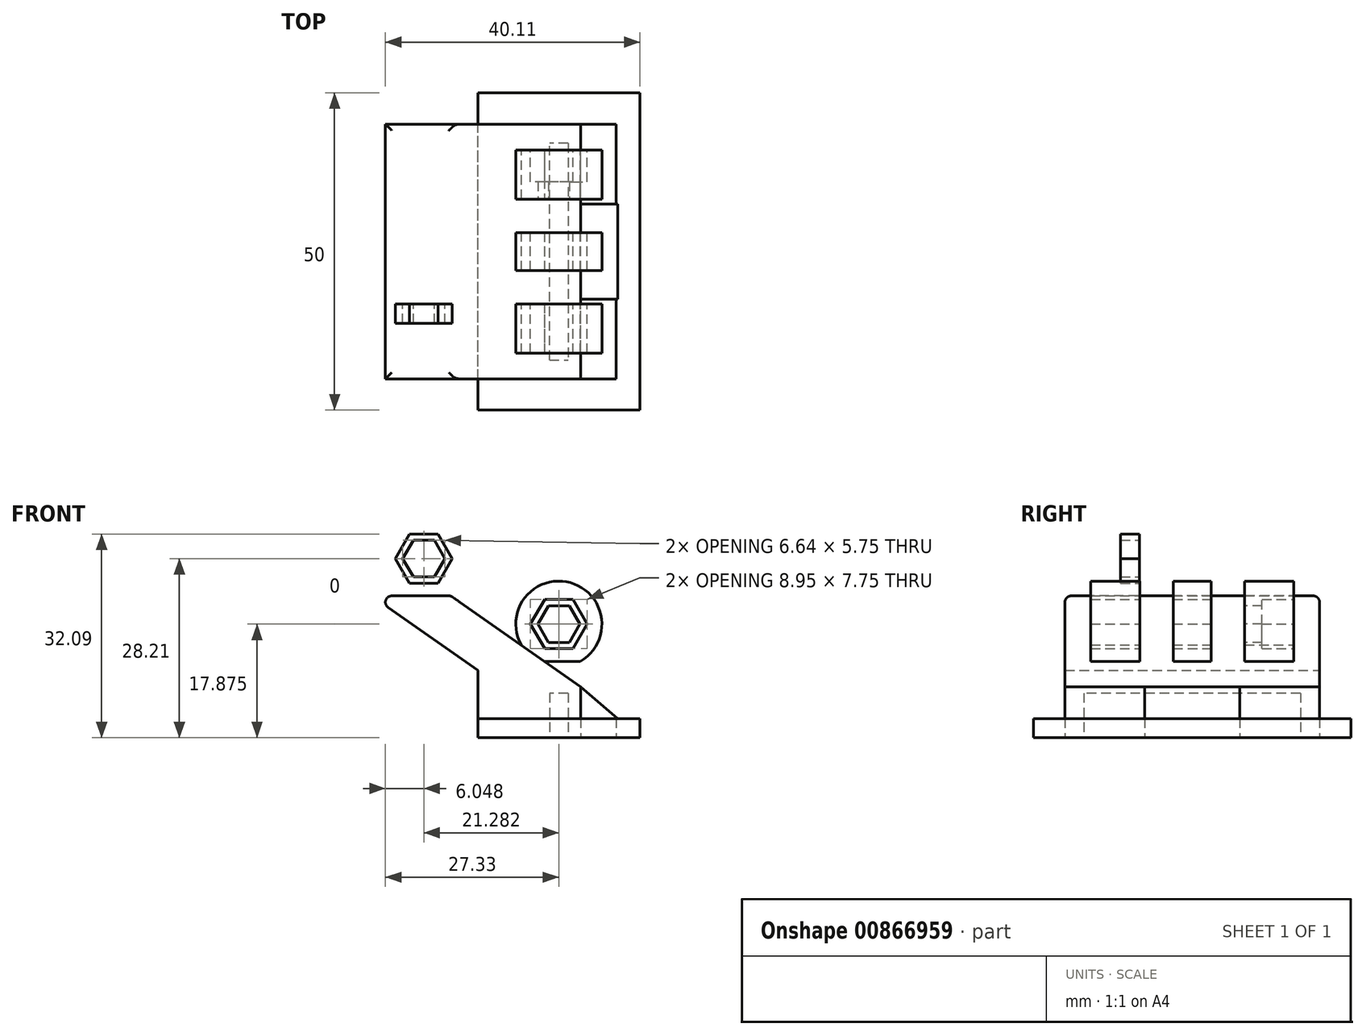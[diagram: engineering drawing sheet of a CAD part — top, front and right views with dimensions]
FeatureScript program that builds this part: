
annotation { "Feature Type Name" : "Feature", "Feature Type Description" : "" }
export const myFeature = defineFeature(function(context is Context, id is Id, definition is map)
    precondition{}
    {
        {
            var Q0;
            Q0=qCreatedBy(makeId("Top.planeOp"),FACE);
            var sketch = newSketch(context, id + "F0", { "sketchPlane" : qUnion([Q0])});
            skLineSegment(sketch, "E0.bottom", {"start": v(12.78, -25) * mm, "end": v(-12.78, -25) * mm});
            skLineSegment(sketch, "E0.top", {"start": v(12.78, 25) * mm, "end": v(-12.77, 25) * mm});
            skLineSegment(sketch, "E0.left", {"start": v(12.78, -25) * mm, "end": v(12.78, 25) * mm});
            skLineSegment(sketch, "E0.right", {"start": v(-12.77, -25) * mm, "end": v(-12.77, 25) * mm});
            skPoint(sketch, "E0.middle", {"position": v(0, 0) * mm});
            skLineSegment(sketch, "E1", {"start": v(-9.02, -25) * mm, "end": v(-9.02, 25) * mm});
            skLineSegment(sketch, "E2", {"start": v(-3.46, 0) * mm, "end": v(3.46, 0) * mm});
            skLineSegment(sketch, "E3", {"start": v(-3.46, -20.07) * mm, "end": v(-3.46, 19.93) * mm});
            skLineSegment(sketch, "E4", {"start": v(-3.46, -20.07) * mm, "end": v(-1.47, -17.07) * mm});
            skLineSegment(sketch, "E5.MirrorCS", {"start": v(-3.46, 20.07) * mm, "end": v(-1.47, 17.07) * mm});
            skLineSegment(sketch, "E6.MirrorCS", {"start": v(3.46, -20.07) * mm, "end": v(1.47, -17.07) * mm});
            skLineSegment(sketch, "E7.MirrorCS", {"start": v(3.46, 20.07) * mm, "end": v(1.47, 17.07) * mm});
            skLineSegment(sketch, "E8", {"start": v(-1.47, -17.07) * mm, "end": v(1.47, -17.07) * mm});
            skLineSegment(sketch, "E9", {"start": v(1.47, 17.07) * mm, "end": v(1.47, -17.07) * mm});
            skLineSegment(sketch, "E10", {"start": v(-1.47, -17.07) * mm, "end": v(-1.47, 17.07) * mm});
            skLineSegment(sketch, "E11", {"start": v(1.47, 17.07) * mm, "end": v(-1.47, 17.07) * mm});
            skLineSegment(sketch, "E12", {"start": v(-12.77, 20.07) * mm, "end": v(12.78, 20.07) * mm});
            skLineSegment(sketch, "E13", {"start": v(-12.77, -20.07) * mm, "end": v(12.78, -20.07) * mm});
            skLineSegment(sketch, "E14", {"start": v(9.02, 25) * mm, "end": v(9.02, -25) * mm});
            skLineSegment(sketch, "E15", {"start": v(3.46, 20.07) * mm, "end": v(3.46, -20.07) * mm});
            skPoint(sketch, "E16.startSnap0", {"position": v(0, 25) * mm});
            skSolve(sketch);
        }
        {
            var Q0;
            {var subQ0=sQuery(id+"F0.wireOp",EDGE,"E0.left");Q0=makeQuery(id+"F0.imprint","IMPRINT",FACE,{"disambiguationData":[TD([[makeQuery(id+"F0.imprint","IMPRINT",EDGE,{"derivedFrom":subQ0}),1.0]])]});}
            var Q1;
            {var subQ1=sQuery(id+"F0.wireOp",EDGE,"uCLvqHpc-epR2-lUNU-6zMB-YpV1tJLCVuEA");var subQ4=sQuery(id+"F0.wireOp",EDGE,"E0.bottom");var subQ5=makeQuery(id+"F0.imprint","INTERSECT",VERTEX,{"derivedFrom":[subQ4,subQ1]});Q1=makeQuery(id+"F0.imprint","IMPRINT",FACE,{"disambiguationData":[TD([[makeQuery(id+"F0.imprint","IMPRINT",EDGE,{"disambiguationData":[TD([[subQ5,-1.0]])],"derivedFrom":subQ4}),-1.0]])]});}
            var Q2;
            {var subQ1=sQuery(id+"F0.wireOp",EDGE,"uCLvqHpc-epR2-lUNU-6zMB-YpV1tJLCVuEA");var subQ5=sQuery(id+"F0.wireOp",EDGE,"E0.top");var subQ8=makeQuery(id+"F0.imprint","INTERSECT",VERTEX,{"derivedFrom":[subQ5,subQ1]});Q2=makeQuery(id+"F0.imprint","IMPRINT",FACE,{"disambiguationData":[TD([[makeQuery(id+"F0.imprint","IMPRINT",EDGE,{"disambiguationData":[TD([[subQ8,-1.0]])],"derivedFrom":subQ5}),1.0]])]});}
            var Q3;
            {var subQ5=sQuery(id+"F0.wireOp",EDGE,"CDGRJo3m-BFBn-T6ZY-9gTP-HfmTZKA6B6aL");Q3=makeQuery(id+"F0.imprint","IMPRINT",FACE,{"disambiguationData":[TD([[makeQuery(id+"F0.imprint","IMPRINT",EDGE,{"derivedFrom":subQ5}),1.0]])]});}
            var Q4;
            {var subQ5=sQuery(id+"F0.wireOp",EDGE,"XeZ3GIGw-x2t7-Umph-tXQI-VwEUVpRtyOsu");Q4=makeQuery(id+"F0.imprint","IMPRINT",FACE,{"disambiguationData":[TD([[makeQuery(id+"F0.imprint","IMPRINT",EDGE,{"derivedFrom":subQ5}),-1.0]])]});}
            var Q5;
            {var subQ2=sQuery(id+"F0.wireOp",EDGE,"E1");var subQ5=sQuery(id+"F0.wireOp",EDGE,"E0.bottom");var subQ8=makeQuery(id+"F0.imprint","INTERSECT",VERTEX,{"derivedFrom":[subQ5,subQ2]});Q5=makeQuery(id+"F0.imprint","IMPRINT",FACE,{"disambiguationData":[TD([[makeQuery(id+"F0.imprint","IMPRINT",EDGE,{"disambiguationData":[TD([[subQ8,1.0]])],"derivedFrom":subQ5}),-1.0]])]});}
            var Q6;
            {var subQ1=sQuery(id+"F0.wireOp",EDGE,"E0.top");var subQ6=sQuery(id+"F0.wireOp",EDGE,"E1");var subQ8=makeQuery(id+"F0.imprint","INTERSECT",VERTEX,{"derivedFrom":[subQ1,subQ6]});Q6=makeQuery(id+"F0.imprint","IMPRINT",FACE,{"disambiguationData":[TD([[makeQuery(id+"F0.imprint","IMPRINT",EDGE,{"disambiguationData":[TD([[subQ8,1.0]])],"derivedFrom":subQ1}),1.0]])]});}
            extrude(context, id + "F1", {"entities" : qUnion([Q0, Q1, Q2, Q3, Q4, Q5, Q6]), "depth" : 3 * mm, "offsetDistance" : 25 * mm});
        }
        {
            var Q0;
            {var subQ0=sQuery(id+"F0.wireOp",EDGE,"E5.MirrorCS");Q0=makeQuery(id+"F0.imprint","IMPRINT",FACE,{"disambiguationData":[TD([[makeQuery(id+"F0.imprint","IMPRINT",EDGE,{"derivedFrom":subQ0}),1.0]])]});}
            var Q1;
            {var subQ5=sQuery(id+"F0.wireOp",EDGE,"E11");Q1=makeQuery(id+"F0.imprint","IMPRINT",FACE,{"disambiguationData":[TD([[makeQuery(id+"F0.imprint","IMPRINT",EDGE,{"derivedFrom":subQ5}),1.0]])]});}
            var Q2;
            {var subQ5=sQuery(id+"F0.wireOp",EDGE,"E8");Q2=makeQuery(id+"F0.imprint","IMPRINT",FACE,{"disambiguationData":[TD([[makeQuery(id+"F0.imprint","IMPRINT",EDGE,{"derivedFrom":subQ5}),1.0]])]});}
            var Q3;
            {var subQ5=sQuery(id+"F0.wireOp",EDGE,"E6.MirrorCS");Q3=makeQuery(id+"F0.imprint","IMPRINT",FACE,{"disambiguationData":[TD([[makeQuery(id+"F0.imprint","IMPRINT",EDGE,{"derivedFrom":subQ5}),-1.0]])]});}
            var Q4;
            {var subQ5=sQuery(id+"F0.wireOp",EDGE,"E4");Q4=makeQuery(id+"F0.imprint","IMPRINT",FACE,{"disambiguationData":[TD([[makeQuery(id+"F0.imprint","IMPRINT",EDGE,{"derivedFrom":subQ5}),1.0]])]});}
            var Q5;
            {var subQ0=sQuery(id+"F0.wireOp",EDGE,"E4");Q5=makeQuery(id+"F0.imprint","IMPRINT",FACE,{"disambiguationData":[TD([[makeQuery(id+"F0.imprint","IMPRINT",EDGE,{"derivedFrom":subQ0}),-1.0]])]});}
            var Q6;
            {var subQ5=sQuery(id+"F0.wireOp",EDGE,"E7.MirrorCS");Q6=makeQuery(id+"F0.imprint","IMPRINT",FACE,{"disambiguationData":[TD([[makeQuery(id+"F0.imprint","IMPRINT",EDGE,{"derivedFrom":subQ5}),1.0]])]});}
            var Q7;
            {var subQ0=sQuery(id+"F0.wireOp",EDGE,"E5.MirrorCS");Q7=makeQuery(id+"F0.imprint","IMPRINT",FACE,{"disambiguationData":[TD([[makeQuery(id+"F0.imprint","IMPRINT",EDGE,{"derivedFrom":subQ0}),-1.0]])]});}
            extrude(context, id + "F2", {"entities" : qUnion([Q0, Q1, Q2, Q3, Q4, Q5, Q6, Q7]), "operationType" : NewBodyOperationType.ADD, "depth" : 8 * mm, "offsetDistance" : 25 * mm});
        }
        {
            var Q0;
            {var subQ5=sQuery(id+"F0.wireOp",EDGE,"E8");Q0=makeQuery(id+"F0.imprint","IMPRINT",FACE,{"disambiguationData":[TD([[makeQuery(id+"F0.imprint","IMPRINT",EDGE,{"derivedFrom":subQ5}),1.0]])]});}
            var Q1;
            {var subQ5=sQuery(id+"F0.wireOp",EDGE,"E11");Q1=makeQuery(id+"F0.imprint","IMPRINT",FACE,{"disambiguationData":[TD([[makeQuery(id+"F0.imprint","IMPRINT",EDGE,{"derivedFrom":subQ5}),1.0]])]});}
            extrude(context, id + "F3", {"entities" : qUnion([Q0, Q1]), "operationType" : NewBodyOperationType.REMOVE, "depth" : 7 * mm, "offsetDistance" : 25 * mm});
        }
        {
            var Q0;
            Q0=qCreatedBy(makeId("Front.planeOp"),FACE);
            var sketch = newSketch(context, id + "F4", { "sketchPlane" : qUnion([Q0])});
            skLineSegment(sketch, "E17", {"start": v(0, 0) * mm, "end": v(0, 11.88) * mm});
            skLineSegment(sketch, "E18", {"start": v(0, 11.88) * mm, "end": v(0, 23.88) * mm});
            skCircle(sketch, "E19", {"center": v(0, 17.88) * mm, "radius": 3.88 * mm});
            skCircle(sketch, "E20.cCircle", {"center": v(0, 17.88) * mm, "radius": 3.88 * mm, "construction": true});
            skLineSegment(sketch, "E20.0", {"start": v(2.24, 14) * mm, "end": v(-2.24, 14) * mm});
            skLineSegment(sketch, "E20.1", {"start": v(-2.24, 14) * mm, "end": v(-4.47, 17.88) * mm});
            skLineSegment(sketch, "E20.2", {"start": v(-4.47, 17.88) * mm, "end": v(-2.24, 21.75) * mm});
            skLineSegment(sketch, "E20.3", {"start": v(-2.24, 21.75) * mm, "end": v(2.24, 21.75) * mm});
            skLineSegment(sketch, "E20.4", {"start": v(2.24, 21.75) * mm, "end": v(4.47, 17.88) * mm});
            skLineSegment(sketch, "E20.5", {"start": v(4.47, 17.88) * mm, "end": v(2.24, 14) * mm});
            skPoint(sketch, "E20.0.midPoint", {"position": v(0, 14) * mm});
            skLineSegment(sketch, "E21.0", {"start": v(-6.78, 17.88) * mm, "end": v(-3.4, 23.75) * mm});
            skLineSegment(sketch, "E21.1", {"start": v(3.4, 23.75) * mm, "end": v(6.78, 17.88) * mm});
            skLineSegment(sketch, "E21.2", {"start": v(6.78, 17.88) * mm, "end": v(3.4, 12) * mm});
            skLineSegment(sketch, "E21.3", {"start": v(-3.4, 23.75) * mm, "end": v(3.4, 23.75) * mm});
            skLineSegment(sketch, "E21.4", {"start": v(3.4, 12) * mm, "end": v(-3.4, 12) * mm});
            skLineSegment(sketch, "E21.5", {"start": v(-3.4, 12) * mm, "end": v(-6.78, 17.88) * mm});
            skLineSegment(sketch, "E22.0", {"start": v(-1.66, 20.75) * mm, "end": v(1.66, 20.75) * mm});
            skLineSegment(sketch, "E22.1", {"start": v(3.32, 17.88) * mm, "end": v(1.66, 15) * mm});
            skLineSegment(sketch, "E22.2", {"start": v(1.66, 15) * mm, "end": v(-1.66, 15) * mm});
            skLineSegment(sketch, "E22.3", {"start": v(1.66, 20.75) * mm, "end": v(3.32, 17.88) * mm});
            skLineSegment(sketch, "E22.4", {"start": v(-1.66, 15) * mm, "end": v(-3.32, 17.88) * mm});
            skLineSegment(sketch, "E22.5", {"start": v(-3.32, 17.88) * mm, "end": v(-1.66, 20.75) * mm});
            skCircle(sketch, "E23", {"center": v(0, 17.88) * mm, "radius": 6.78 * mm});
            skSolve(sketch);
        }
        {
            var Q0;
            {var subQ1=sQuery(id+"F4.wireOp",EDGE,"E21.1");Q0=makeQuery(id+"F4.imprint","IMPRINT",FACE,{"disambiguationData":[TD([[makeQuery(id+"F4.imprint","IMPRINT",EDGE,{"derivedFrom":subQ1}),-1.0]])]});}
            var Q1;
            {var subQ14=sQuery(id+"F4.wireOp",EDGE,"E21.0");Q1=makeQuery(id+"F4.imprint","IMPRINT",FACE,{"disambiguationData":[TD([[makeQuery(id+"F4.imprint","IMPRINT",EDGE,{"derivedFrom":subQ14}),-1.0]])]});}
            var Q2;
            {var subQ0=sQuery(id+"F4.wireOp",EDGE,"E21.0");Q2=makeQuery(id+"F4.imprint","IMPRINT",FACE,{"disambiguationData":[TD([[makeQuery(id+"F4.imprint","IMPRINT",EDGE,{"derivedFrom":subQ0}),1.0]])]});}
            var Q3;
            {var subQ0=sQuery(id+"F4.wireOp",EDGE,"E21.5");Q3=makeQuery(id+"F4.imprint","IMPRINT",FACE,{"disambiguationData":[TD([[makeQuery(id+"F4.imprint","IMPRINT",EDGE,{"derivedFrom":subQ0}),1.0]])]});}
            var Q4;
            {var subQ0=sQuery(id+"F4.wireOp",EDGE,"E21.2");Q4=makeQuery(id+"F4.imprint","IMPRINT",FACE,{"disambiguationData":[TD([[makeQuery(id+"F4.imprint","IMPRINT",EDGE,{"derivedFrom":subQ0}),1.0]])]});}
            var Q5;
            {var subQ0=sQuery(id+"F4.wireOp",EDGE,"E21.1");Q5=makeQuery(id+"F4.imprint","IMPRINT",FACE,{"disambiguationData":[TD([[makeQuery(id+"F4.imprint","IMPRINT",EDGE,{"derivedFrom":subQ0}),1.0]])]});}
            var Q6;
            {var subQ0=sQuery(id+"F4.wireOp",EDGE,"E21.3");var subQ1=makeQuery(id+"F4.imprint","INTERSECT",VERTEX,{"derivedFrom":[sQuery(id+"F4.wireOp",EDGE,"E18"),subQ0]});Q6=makeQuery(id+"F4.imprint","IMPRINT",FACE,{"disambiguationData":[TD([[makeQuery(id+"F4.imprint","IMPRINT",EDGE,{"disambiguationData":[TD([[subQ1,1.0]])],"derivedFrom":subQ0}),1.0]])]});}
            extrude(context, id + "F5", {"entities" : qUnion([Q0, Q1, Q2, Q3, Q4, Q5, Q6]), "operationType" : NewBodyOperationType.ADD, "depth" : 16 * mm, "offsetDistance" : 25 * mm, "hasSecondDirection" : true, "secondDirectionOppositeDirection" : true, "secondDirectionDepth" : 16 * mm});
        }
        {
            var Q0;
            {var subQ0=sQuery(id+"F4.wireOp",EDGE,"E20.2");var subQ1=sQuery(id+"F4.wireOp",EDGE,"E19");var subQ2=makeQuery(id+"F4.imprint","INTERSECT",VERTEX,{"derivedFrom":[subQ1,subQ0]});Q0=makeQuery(id+"F4.imprint","IMPRINT",FACE,{"disambiguationData":[TD([[makeQuery(id+"F4.imprint","IMPRINT",EDGE,{"disambiguationData":[TD([[subQ2,-1.0]])],"derivedFrom":subQ1}),-1.0]])]});}
            var Q1;
            {var subQ0=sQuery(id+"F4.wireOp",EDGE,"E20.2");var subQ3=sQuery(id+"F4.wireOp",EDGE,"E20.3");var subQ5=makeQuery(id+"F4.imprint","INTERSECT",VERTEX,{"derivedFrom":[subQ0,subQ3]});Q1=makeQuery(id+"F4.imprint","IMPRINT",FACE,{"disambiguationData":[TD([[makeQuery(id+"F4.imprint","IMPRINT",EDGE,{"disambiguationData":[TD([[subQ5,1.0]])],"derivedFrom":subQ0}),-1.0]])]});}
            var Q2;
            {var subQ11=sQuery(id+"F4.wireOp",EDGE,"E22.4");Q2=makeQuery(id+"F4.imprint","IMPRINT",FACE,{"disambiguationData":[TD([[makeQuery(id+"F4.imprint","IMPRINT",EDGE,{"derivedFrom":subQ11}),1.0]])]});}
            var Q3;
            {var subQ11=sQuery(id+"F4.wireOp",EDGE,"E22.1");Q3=makeQuery(id+"F4.imprint","IMPRINT",FACE,{"disambiguationData":[TD([[makeQuery(id+"F4.imprint","IMPRINT",EDGE,{"derivedFrom":subQ11}),1.0]])]});}
            var Q4;
            {var subQ0=sQuery(id+"F4.wireOp",EDGE,"E20.4");var subQ3=sQuery(id+"F4.wireOp",EDGE,"E20.3");var subQ5=makeQuery(id+"F4.imprint","INTERSECT",VERTEX,{"derivedFrom":[subQ3,subQ0]});Q4=makeQuery(id+"F4.imprint","IMPRINT",FACE,{"disambiguationData":[TD([[makeQuery(id+"F4.imprint","IMPRINT",EDGE,{"disambiguationData":[TD([[subQ5,-1.0]])],"derivedFrom":subQ0}),-1.0]])]});}
            var Q5;
            {var subQ0=sQuery(id+"F4.wireOp",EDGE,"E20.4");var subQ1=sQuery(id+"F4.wireOp",EDGE,"E19");var subQ2=makeQuery(id+"F4.imprint","INTERSECT",VERTEX,{"derivedFrom":[subQ1,subQ0]});Q5=makeQuery(id+"F4.imprint","IMPRINT",FACE,{"disambiguationData":[TD([[makeQuery(id+"F4.imprint","IMPRINT",EDGE,{"disambiguationData":[TD([[subQ2,1.0]])],"derivedFrom":subQ1}),-1.0]])]});}
            var Q6;
            {var subQ0=sQuery(id+"F4.wireOp",EDGE,"E20.5");var subQ3=sQuery(id+"F4.wireOp",EDGE,"E20.0");var subQ5=makeQuery(id+"F4.imprint","INTERSECT",VERTEX,{"derivedFrom":[subQ3,subQ0]});Q6=makeQuery(id+"F4.imprint","IMPRINT",FACE,{"disambiguationData":[TD([[makeQuery(id+"F4.imprint","IMPRINT",EDGE,{"disambiguationData":[TD([[subQ5,1.0]])],"derivedFrom":subQ0}),-1.0]])]});}
            var Q7;
            {var subQ0=sQuery(id+"F4.wireOp",EDGE,"E20.1");var subQ3=sQuery(id+"F4.wireOp",EDGE,"E20.0");var subQ5=makeQuery(id+"F4.imprint","INTERSECT",VERTEX,{"derivedFrom":[subQ3,subQ0]});Q7=makeQuery(id+"F4.imprint","IMPRINT",FACE,{"disambiguationData":[TD([[makeQuery(id+"F4.imprint","IMPRINT",EDGE,{"disambiguationData":[TD([[subQ5,-1.0]])],"derivedFrom":subQ0}),-1.0]])]});}
            extrude(context, id + "F6", {"entities" : qUnion([Q0, Q1, Q2, Q3, Q4, Q5, Q6, Q7]), "depth" : (16 - 4.7) * mm, "offsetDistance" : 25 * mm, "hasSecondDirection" : true, "secondDirectionOppositeDirection" : false, "secondDirectionDepth" : 8.3 * mm});
        }
        {
            var Q0;
            {var subQ0=sQuery(id+"F4.wireOp",EDGE,"E20.4");var subQ3=sQuery(id+"F4.wireOp",EDGE,"E20.3");var subQ5=makeQuery(id+"F4.imprint","INTERSECT",VERTEX,{"derivedFrom":[subQ3,subQ0]});Q0=makeQuery(id+"F4.imprint","IMPRINT",FACE,{"disambiguationData":[TD([[makeQuery(id+"F4.imprint","IMPRINT",EDGE,{"disambiguationData":[TD([[subQ5,-1.0]])],"derivedFrom":subQ0}),-1.0]])]});}
            var Q1;
            {var subQ11=sQuery(id+"F4.wireOp",EDGE,"E22.1");Q1=makeQuery(id+"F4.imprint","IMPRINT",FACE,{"disambiguationData":[TD([[makeQuery(id+"F4.imprint","IMPRINT",EDGE,{"derivedFrom":subQ11}),1.0]])]});}
            var Q2;
            {var subQ11=sQuery(id+"F4.wireOp",EDGE,"E22.4");Q2=makeQuery(id+"F4.imprint","IMPRINT",FACE,{"disambiguationData":[TD([[makeQuery(id+"F4.imprint","IMPRINT",EDGE,{"derivedFrom":subQ11}),1.0]])]});}
            var Q3;
            {var subQ0=sQuery(id+"F4.wireOp",EDGE,"E20.2");var subQ3=sQuery(id+"F4.wireOp",EDGE,"E20.3");var subQ5=makeQuery(id+"F4.imprint","INTERSECT",VERTEX,{"derivedFrom":[subQ0,subQ3]});Q3=makeQuery(id+"F4.imprint","IMPRINT",FACE,{"disambiguationData":[TD([[makeQuery(id+"F4.imprint","IMPRINT",EDGE,{"disambiguationData":[TD([[subQ5,1.0]])],"derivedFrom":subQ0}),-1.0]])]});}
            var Q4;
            {var subQ0=sQuery(id+"F4.wireOp",EDGE,"E20.4");var subQ1=sQuery(id+"F4.wireOp",EDGE,"E19");var subQ2=makeQuery(id+"F4.imprint","INTERSECT",VERTEX,{"derivedFrom":[subQ1,subQ0]});Q4=makeQuery(id+"F4.imprint","IMPRINT",FACE,{"disambiguationData":[TD([[makeQuery(id+"F4.imprint","IMPRINT",EDGE,{"disambiguationData":[TD([[subQ2,1.0]])],"derivedFrom":subQ1}),-1.0]])]});}
            var Q5;
            {var subQ0=sQuery(id+"F4.wireOp",EDGE,"E20.5");var subQ3=sQuery(id+"F4.wireOp",EDGE,"E20.0");var subQ5=makeQuery(id+"F4.imprint","INTERSECT",VERTEX,{"derivedFrom":[subQ3,subQ0]});Q5=makeQuery(id+"F4.imprint","IMPRINT",FACE,{"disambiguationData":[TD([[makeQuery(id+"F4.imprint","IMPRINT",EDGE,{"disambiguationData":[TD([[subQ5,1.0]])],"derivedFrom":subQ0}),-1.0]])]});}
            var Q6;
            {var subQ0=sQuery(id+"F4.wireOp",EDGE,"E20.1");var subQ3=sQuery(id+"F4.wireOp",EDGE,"E20.0");var subQ5=makeQuery(id+"F4.imprint","INTERSECT",VERTEX,{"derivedFrom":[subQ3,subQ0]});Q6=makeQuery(id+"F4.imprint","IMPRINT",FACE,{"disambiguationData":[TD([[makeQuery(id+"F4.imprint","IMPRINT",EDGE,{"disambiguationData":[TD([[subQ5,-1.0]])],"derivedFrom":subQ0}),-1.0]])]});}
            var Q7;
            {var subQ0=sQuery(id+"F4.wireOp",EDGE,"E20.2");var subQ1=sQuery(id+"F4.wireOp",EDGE,"E19");var subQ2=makeQuery(id+"F4.imprint","INTERSECT",VERTEX,{"derivedFrom":[subQ1,subQ0]});Q7=makeQuery(id+"F4.imprint","IMPRINT",FACE,{"disambiguationData":[TD([[makeQuery(id+"F4.imprint","IMPRINT",EDGE,{"disambiguationData":[TD([[subQ2,-1.0]])],"derivedFrom":subQ1}),-1.0]])]});}
            extrude(context, id + "F7", {"entities" : qUnion([Q0, Q1, Q2, Q3, Q4, Q5, Q6, Q7]), "operationType" : NewBodyOperationType.ADD, "oppositeDirection" : true, "depth" : (16 - 5) * mm, "offsetDistance" : 25 * mm, "hasSecondDirection" : true, "secondDirectionOppositeDirection" : true, "secondDirectionDepth" : 8.25 * mm});
        }
        {
            var Q0;
            {var subQ0=sQuery(id+"F4.wireOp",EDGE,"E21.0");Q0=makeQuery(id+"F4.imprint","IMPRINT",FACE,{"disambiguationData":[TD([[makeQuery(id+"F4.imprint","IMPRINT",EDGE,{"derivedFrom":subQ0}),1.0]])]});}
            var Q1;
            {var subQ14=sQuery(id+"F4.wireOp",EDGE,"E21.0");Q1=makeQuery(id+"F4.imprint","IMPRINT",FACE,{"disambiguationData":[TD([[makeQuery(id+"F4.imprint","IMPRINT",EDGE,{"derivedFrom":subQ14}),-1.0]])]});}
            var Q2;
            {var subQ1=sQuery(id+"F4.wireOp",EDGE,"E21.1");Q2=makeQuery(id+"F4.imprint","IMPRINT",FACE,{"disambiguationData":[TD([[makeQuery(id+"F4.imprint","IMPRINT",EDGE,{"derivedFrom":subQ1}),-1.0]])]});}
            var Q3;
            {var subQ0=sQuery(id+"F4.wireOp",EDGE,"E21.3");var subQ1=makeQuery(id+"F4.imprint","INTERSECT",VERTEX,{"derivedFrom":[sQuery(id+"F4.wireOp",EDGE,"E18"),subQ0]});Q3=makeQuery(id+"F4.imprint","IMPRINT",FACE,{"disambiguationData":[TD([[makeQuery(id+"F4.imprint","IMPRINT",EDGE,{"disambiguationData":[TD([[subQ1,1.0]])],"derivedFrom":subQ0}),1.0]])]});}
            var Q4;
            {var subQ0=sQuery(id+"F4.wireOp",EDGE,"E21.1");Q4=makeQuery(id+"F4.imprint","IMPRINT",FACE,{"disambiguationData":[TD([[makeQuery(id+"F4.imprint","IMPRINT",EDGE,{"derivedFrom":subQ0}),1.0]])]});}
            var Q5;
            {var subQ0=sQuery(id+"F4.wireOp",EDGE,"E21.5");Q5=makeQuery(id+"F4.imprint","IMPRINT",FACE,{"disambiguationData":[TD([[makeQuery(id+"F4.imprint","IMPRINT",EDGE,{"derivedFrom":subQ0}),1.0]])]});}
            var Q6;
            {var subQ0=sQuery(id+"F4.wireOp",EDGE,"E21.2");Q6=makeQuery(id+"F4.imprint","IMPRINT",FACE,{"disambiguationData":[TD([[makeQuery(id+"F4.imprint","IMPRINT",EDGE,{"derivedFrom":subQ0}),1.0]])]});}
            extrude(context, id + "F8", {"entities" : qUnion([Q0, Q1, Q2, Q3, Q4, Q5, Q6]), "operationType" : NewBodyOperationType.REMOVE, "oppositeDirection" : true, "depth" : 8.25 * mm, "offsetDistance" : 25 * mm, "hasSecondDirection" : true, "secondDirectionOppositeDirection" : true, "secondDirectionDepth" : 3 * mm});
        }
        {
            var Q0;
            {var subQ1=sQuery(id+"F4.wireOp",EDGE,"E21.1");Q0=makeQuery(id+"F4.imprint","IMPRINT",FACE,{"disambiguationData":[TD([[makeQuery(id+"F4.imprint","IMPRINT",EDGE,{"derivedFrom":subQ1}),-1.0]])]});}
            var Q1;
            {var subQ0=sQuery(id+"F4.wireOp",EDGE,"E21.3");var subQ1=makeQuery(id+"F4.imprint","INTERSECT",VERTEX,{"derivedFrom":[sQuery(id+"F4.wireOp",EDGE,"E18"),subQ0]});Q1=makeQuery(id+"F4.imprint","IMPRINT",FACE,{"disambiguationData":[TD([[makeQuery(id+"F4.imprint","IMPRINT",EDGE,{"disambiguationData":[TD([[subQ1,1.0]])],"derivedFrom":subQ0}),1.0]])]});}
            var Q2;
            {var subQ14=sQuery(id+"F4.wireOp",EDGE,"E21.0");Q2=makeQuery(id+"F4.imprint","IMPRINT",FACE,{"disambiguationData":[TD([[makeQuery(id+"F4.imprint","IMPRINT",EDGE,{"derivedFrom":subQ14}),-1.0]])]});}
            var Q3;
            {var subQ0=sQuery(id+"F4.wireOp",EDGE,"E21.1");Q3=makeQuery(id+"F4.imprint","IMPRINT",FACE,{"disambiguationData":[TD([[makeQuery(id+"F4.imprint","IMPRINT",EDGE,{"derivedFrom":subQ0}),1.0]])]});}
            var Q4;
            {var subQ0=sQuery(id+"F4.wireOp",EDGE,"E21.2");Q4=makeQuery(id+"F4.imprint","IMPRINT",FACE,{"disambiguationData":[TD([[makeQuery(id+"F4.imprint","IMPRINT",EDGE,{"derivedFrom":subQ0}),1.0]])]});}
            var Q5;
            {var subQ0=sQuery(id+"F4.wireOp",EDGE,"E21.0");Q5=makeQuery(id+"F4.imprint","IMPRINT",FACE,{"disambiguationData":[TD([[makeQuery(id+"F4.imprint","IMPRINT",EDGE,{"derivedFrom":subQ0}),1.0]])]});}
            var Q6;
            {var subQ0=sQuery(id+"F4.wireOp",EDGE,"E21.5");Q6=makeQuery(id+"F4.imprint","IMPRINT",FACE,{"disambiguationData":[TD([[makeQuery(id+"F4.imprint","IMPRINT",EDGE,{"derivedFrom":subQ0}),1.0]])]});}
            extrude(context, id + "F9", {"entities" : qUnion([Q0, Q1, Q2, Q3, Q4, Q5, Q6]), "operationType" : NewBodyOperationType.REMOVE, "depth" : 8.25 * mm, "offsetDistance" : 25 * mm, "hasSecondDirection" : true, "secondDirectionOppositeDirection" : false, "secondDirectionDepth" : 3 * mm});
        }
        {
            var Q0;
            Q0=qCreatedBy(makeId("Front.planeOp"),FACE);
            var sketch = newSketch(context, id + "F10", { "sketchPlane" : qUnion([Q0])});
            skLineSegment(sketch, "E24", {"start": v(0, 0) * mm, "end": v(0, 8) * mm});
            skLineSegment(sketch, "E25", {"start": v(0, 8) * mm, "end": v(-3.47, 8) * mm});
            skLineSegment(sketch, "E26", {"start": v(-3.47, 8) * mm, "end": v(-23.95, 22.33) * mm});
            skLineSegment(sketch, "E27", {"start": v(-23.95, 22.33) * mm, "end": v(-23.95, 8) * mm});
            skLineSegment(sketch, "E28", {"start": v(-23.95, 8) * mm, "end": v(-3.47, 8) * mm});
            skLineSegment(sketch, "E29", {"start": v(0, 0) * mm, "end": v(-16.12, 0) * mm});
            skLineSegment(sketch, "E30", {"start": v(0, 0) * mm, "end": v(12.75, 0) * mm});
            skLineSegment(sketch, "E31", {"start": v(0, -2.3) * mm, "end": v(3.46, -2.3) * mm});
            skLineSegment(sketch, "E32", {"start": v(3.46, -2.3) * mm, "end": v(3.46, 0) * mm});
            skLineSegment(sketch, "E33", {"start": v(3.46, 0) * mm, "end": v(3.46, 8) * mm});
            skLineSegment(sketch, "E34", {"start": v(3.46, 8) * mm, "end": v(12.75, 0) * mm});
            skSolve(sketch);
        }
        {
            var Q0;
            Q0=makeQuery(id+"F2.opExtrude","CAP_FACE",FACE,{"disambiguationData":[OSD([sQuery(id+"F0.wireOp",EDGE,"E1"),sQuery(id+"F0.wireOp",EDGE,"ergWaCc5-PQMk-BUm5-Xr42-2uykUVSqbSGA"),sQuery(id+"F0.wireOp",EDGE,"E12"),sQuery(id+"F0.wireOp",EDGE,"E13")])],"isStart":false});
            var Q1;
            Q1=sQuery(id+"F10.wireOp",EDGE,"E26");
            sweep(context, id + "F11", {"operationType" : NewBodyOperationType.ADD, "profiles" : qUnion([Q0]), "path" : qUnion([Q1])});
        }
        {
            var Q0;
            Q0=makeQuery(id+"F8.boolean.opBoolean","SPLIT",BODY,{"disambiguationData":[OD(0.0)],"derivedFrom":makeQuery(id+"F5.opExtrude","SWEPT_BODY",BODY,{"disambiguationData":[OSD([sQuery(id+"F4.wireOp",EDGE,"E20.0"),sQuery(id+"F4.wireOp",EDGE,"E20.1"),sQuery(id+"F4.wireOp",EDGE,"E20.2"),sQuery(id+"F4.wireOp",EDGE,"E20.3"),sQuery(id+"F4.wireOp",EDGE,"E20.4"),sQuery(id+"F4.wireOp",EDGE,"E20.5"),sQuery(id+"F4.wireOp",EDGE,"E21.4"),sQuery(id+"F4.wireOp",EDGE,"E23")])]})});
            var Q1;
            Q1=makeQuery(id+"F9.boolean.opBoolean","SPLIT",BODY,{"disambiguationData":[OD(0.0)],"derivedFrom":makeQuery(id+"F8.boolean.opBoolean","SPLIT",BODY,{"disambiguationData":[OD(1.0)],"derivedFrom":makeQuery(id+"F5.opExtrude","SWEPT_BODY",BODY,{"disambiguationData":[OSD([sQuery(id+"F4.wireOp",EDGE,"E20.0"),sQuery(id+"F4.wireOp",EDGE,"E20.1"),sQuery(id+"F4.wireOp",EDGE,"E20.2"),sQuery(id+"F4.wireOp",EDGE,"E20.3"),sQuery(id+"F4.wireOp",EDGE,"E20.4"),sQuery(id+"F4.wireOp",EDGE,"E20.5"),sQuery(id+"F4.wireOp",EDGE,"E21.4"),sQuery(id+"F4.wireOp",EDGE,"E23")])]})})});
            var Q2;
            Q2=makeQuery(id+"F9.boolean.opBoolean","SPLIT",BODY,{"disambiguationData":[OD(1.0)],"derivedFrom":makeQuery(id+"F8.boolean.opBoolean","SPLIT",BODY,{"disambiguationData":[OD(1.0)],"derivedFrom":makeQuery(id+"F5.opExtrude","SWEPT_BODY",BODY,{"disambiguationData":[OSD([sQuery(id+"F4.wireOp",EDGE,"E20.0"),sQuery(id+"F4.wireOp",EDGE,"E20.1"),sQuery(id+"F4.wireOp",EDGE,"E20.2"),sQuery(id+"F4.wireOp",EDGE,"E20.3"),sQuery(id+"F4.wireOp",EDGE,"E20.4"),sQuery(id+"F4.wireOp",EDGE,"E20.5"),sQuery(id+"F4.wireOp",EDGE,"E21.4"),sQuery(id+"F4.wireOp",EDGE,"E23")])]})})});
            var Q3;
            Q3=makeQuery(id+"F7.opExtrude","SWEPT_BODY",BODY,{"disambiguationData":[OSD([sQuery(id+"F4.wireOp",EDGE,"E20.0"),sQuery(id+"F4.wireOp",EDGE,"E20.1"),sQuery(id+"F4.wireOp",EDGE,"E20.2"),sQuery(id+"F4.wireOp",EDGE,"E20.3"),sQuery(id+"F4.wireOp",EDGE,"E20.4"),sQuery(id+"F4.wireOp",EDGE,"E20.5"),sQuery(id+"F4.wireOp",EDGE,"E22.0"),sQuery(id+"F4.wireOp",EDGE,"E22.1"),sQuery(id+"F4.wireOp",EDGE,"E22.2"),sQuery(id+"F4.wireOp",EDGE,"E22.3"),sQuery(id+"F4.wireOp",EDGE,"E22.4"),sQuery(id+"F4.wireOp",EDGE,"E22.5")])]});
            var Q4;
            Q4=makeQuery(id+"F6.opExtrude","SWEPT_BODY",BODY,{"disambiguationData":[OSD([sQuery(id+"F4.wireOp",EDGE,"E20.0"),sQuery(id+"F4.wireOp",EDGE,"E20.1"),sQuery(id+"F4.wireOp",EDGE,"E20.2"),sQuery(id+"F4.wireOp",EDGE,"E20.3"),sQuery(id+"F4.wireOp",EDGE,"E20.4"),sQuery(id+"F4.wireOp",EDGE,"E20.5"),sQuery(id+"F4.wireOp",EDGE,"E22.0"),sQuery(id+"F4.wireOp",EDGE,"E22.1"),sQuery(id+"F4.wireOp",EDGE,"E22.2"),sQuery(id+"F4.wireOp",EDGE,"E22.3"),sQuery(id+"F4.wireOp",EDGE,"E22.4"),sQuery(id+"F4.wireOp",EDGE,"E22.5")])]});
            transform(context, id + "F12", {"entities" : qUnion([Q0, Q1, Q2, Q3, Q4]), "transformType" : TransformType.TRANSLATION_3D, "dx" : -21.28 * mm, "dy" : 0 * mm, "dz" : 10.34 * mm, "makeCopy" : false});
        }
        {
            var Q0;
            {var subQ0=sQuery(id+"F0.wireOp",EDGE,"E12");var subQ1=sQuery(id+"F0.wireOp",EDGE,"E0.right");var subQ2=makeQuery(id+"F0.imprint","INTERSECT",VERTEX,{"derivedFrom":[subQ1,subQ0]});Q0=makeQuery(id+"F0.imprint","IMPRINT",FACE,{"disambiguationData":[TD([[makeQuery(id+"F0.imprint","IMPRINT",EDGE,{"disambiguationData":[TD([[subQ2,1.0]])],"derivedFrom":subQ1}),-1.0]])]});}
            extrude(context, id + "F13", {"entities" : qUnion([Q0]), "operationType" : NewBodyOperationType.ADD, "depth" : 11 * mm, "offsetDistance" : 25 * mm});
        }
        {
            var Q0;
            {var subQ0=sQuery(id+"F10.wireOp",EDGE,"E34");Q0=makeQuery(id+"F10.imprint","IMPRINT",FACE,{"disambiguationData":[TD([[makeQuery(id+"F10.imprint","IMPRINT",EDGE,{"derivedFrom":subQ0}),-1.0]])]});}
            extrude(context, id + "F14", {"entities" : qUnion([Q0]), "operationType" : NewBodyOperationType.ADD, "depth" : 7.5 * mm, "offsetDistance" : 25 * mm, "hasSecondDirection" : true, "secondDirectionOppositeDirection" : true, "secondDirectionDepth" : 7.5 * mm});
        }
        {
            var Q0;
            Q0=makeQuery(id+"F11.opSweep","CAP_EDGE",EDGE,{"disambiguationData":[OSD([sQuery(id+"F0.wireOp",EDGE,"E1"),sQuery(id+"F10.wireOp",VERTEX,"E26.end")])],"isStart":false});
            var Q1;
            Q1=makeQuery(id+"F11.opSweep","CAP_EDGE",EDGE,{"disambiguationData":[OSD([sQuery(id+"F0.wireOp",EDGE,"ergWaCc5-PQMk-BUm5-Xr42-2uykUVSqbSGA"),sQuery(id+"F10.wireOp",VERTEX,"E26.end")])],"isStart":false});
            fillet(context, id + "F15", {"entities" : qUnion([Q0, Q1]), "radius" : 1 * mm, "tangentPropagation" : true, "allowEdgeOverflow" : false});
        }
    });
